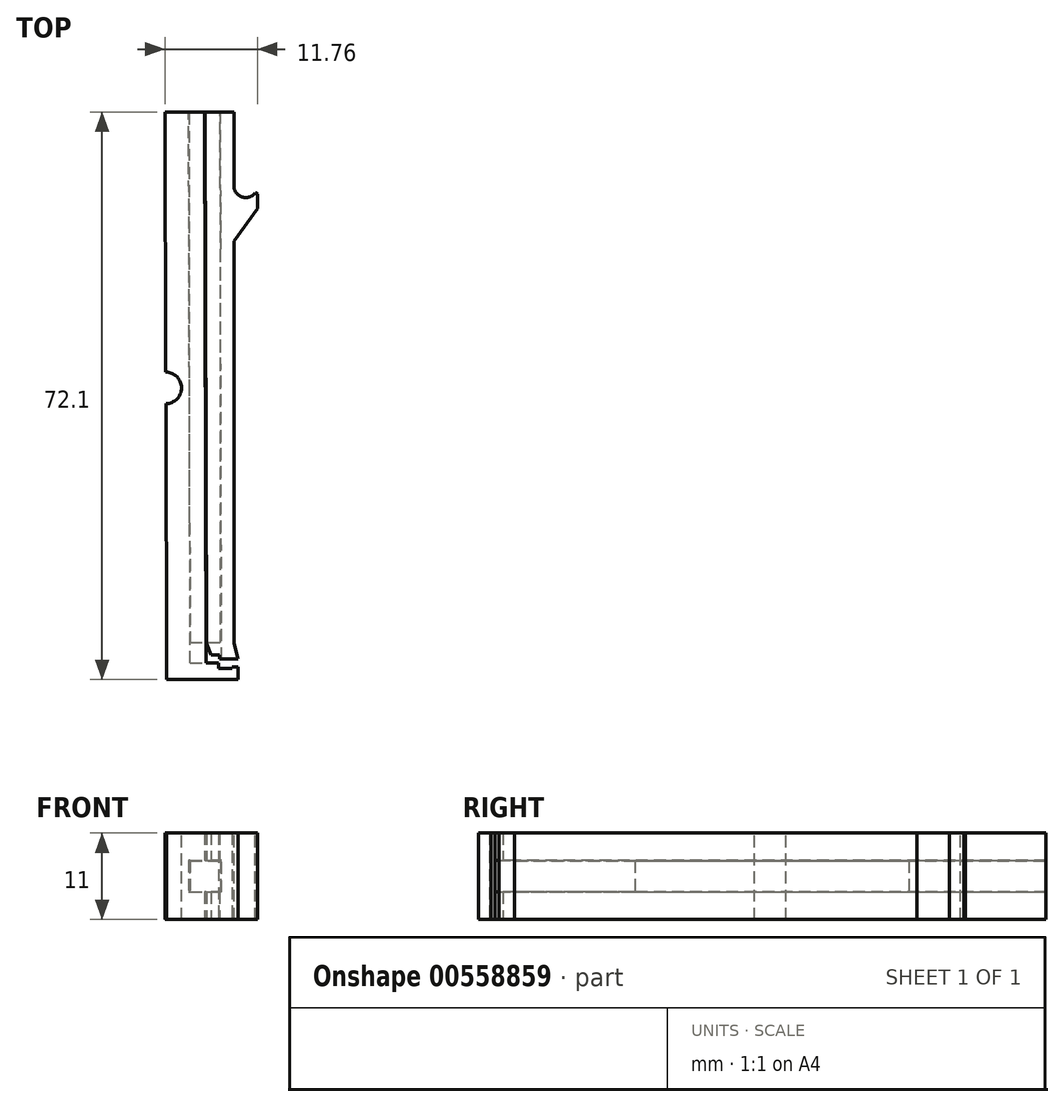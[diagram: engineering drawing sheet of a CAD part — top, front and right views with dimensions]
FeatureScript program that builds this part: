
annotation { "Feature Type Name" : "Feature", "Feature Type Description" : "" }
export const myFeature = defineFeature(function(context is Context, id is Id, definition is map)
    precondition{}
    {
        {
            var Q0;
            Q0=qCreatedBy(makeId("Top.planeOp"),FACE);
            var sketch = newSketch(context, id + "F0", { "sketchPlane" : qUnion([Q0])});
            skLineSegment(sketch, "E0", {"start": v(-25.83, -4.71) * mm, "end": v(-26.63, -4.71) * mm});
            skLineSegment(sketch, "E1", {"start": v(-25.84, -3.71) * mm, "end": v(-28.23, -3.71) * mm});
            skLineSegment(sketch, "E2", {"start": v(-25.83, -4.71) * mm, "end": v(-25.83, -6.31) * mm});
            skLineSegment(sketch, "E3", {"start": v(-26.63, -4.71) * mm, "end": v(-26.63, -4.91) * mm});
            skLineSegment(sketch, "E4", {"start": v(-26.63, -4.91) * mm, "end": v(-28.33, -4.91) * mm});
            skLineSegment(sketch, "E5", {"start": v(-28.33, -4.91) * mm, "end": v(-28.33, -4.71) * mm});
            skLineSegment(sketch, "E6", {"start": v(-25.84, -3.71) * mm, "end": v(-26.38, -1.71) * mm});
            skLineSegment(sketch, "E7", {"start": v(-25.83, -6.31) * mm, "end": v(-31.04, -6.31) * mm});
            skLineSegment(sketch, "E8", {"start": v(-28.33, -4.71) * mm, "end": v(-28.33, -4.21) * mm});
            skLineSegment(sketch, "E9", {"start": v(-28.33, -4.21) * mm, "end": v(-29.93, -4.21) * mm});
            skLineSegment(sketch, "E10", {"start": v(-28.23, -3.71) * mm, "end": v(-28.23, -3.21) * mm});
            skLineSegment(sketch, "E11", {"start": v(-28.23, -3.21) * mm, "end": v(-29.28, -3.21) * mm});
            skLineSegment(sketch, "E12", {"start": v(-29.93, -4.21) * mm, "end": v(-30.14, 65.79) * mm});
            skLineSegment(sketch, "E13", {"start": v(-30.14, 65.79) * mm, "end": v(-35.14, 65.77) * mm});
            skLineSegment(sketch, "E14", {"start": v(-35.14, 65.77) * mm, "end": v(-34.93, -6.31) * mm});
            skLineSegment(sketch, "E15", {"start": v(-34.93, -6.31) * mm, "end": v(-31.04, -6.31) * mm});
            skPoint(sketch, "E16.trimOffspring.end.orphan", {"position": v(-30.14, -4.71) * mm});
            skLineSegment(sketch, "E17", {"start": v(-26.38, -1.71) * mm, "end": v(-26.38, 65.79) * mm});
            skLineSegment(sketch, "E18", {"start": v(-26.38, 65.79) * mm, "end": v(-30.04, 65.79) * mm});
            skLineSegment(sketch, "E19", {"start": v(-30.04, 65.79) * mm, "end": v(-29.84, -1.71) * mm});
            skLineSegment(sketch, "E20", {"start": v(-29.84, -1.71) * mm, "end": v(-29.28, -3.21) * mm});
            skPoint(sketch, "E21.end.orphan", {"position": v(-29.32, -1.71) * mm});
            skSolve(sketch);
        }
        {
            var Q0;
            Q0 = qSketchRegion(id + "F0", true);
            extrude(context, id + "F1", {"entities" : qUnion([Q0]), "depth" : 11 * mm, "offsetDistance" : 25 * mm});
        }
        {
            var Q0;
            Q0=makeQuery(id+"F1.opExtrude","SWEPT_FACE",FACE,{"disambiguationData":[OSD([sQuery(id+"F0.wireOp",EDGE,"E13")])]});
            var sketch = newSketch(context, id + "F2", { "sketchPlane" : qUnion([Q0])});
            skLineSegment(sketch, "E22.bottom", {"start": v(31.95, 7.5) * mm, "end": v(27.95, 7.5) * mm});
            skLineSegment(sketch, "E22.top", {"start": v(31.95, 3.5) * mm, "end": v(27.95, 3.5) * mm});
            skLineSegment(sketch, "E22.left", {"start": v(31.95, 7.5) * mm, "end": v(31.95, 3.5) * mm});
            skLineSegment(sketch, "E22.right", {"start": v(27.95, 7.5) * mm, "end": v(27.95, 3.5) * mm});
            skPoint(sketch, "E22.middle", {"position": v(29.95, 5.5) * mm});
            skSolve(sketch);
        }
        {
            var Q0;
            Q0 = qSketchRegion(id + "F2", true);
            var Q1;
            Q1=makeQuery(id+"F1.opExtrude","SWEPT_FACE",FACE,{"disambiguationData":[OSD([sQuery(id+"F0.wireOp",EDGE,"E9")])]});
            extrude(context, id + "F3", {"entities" : qUnion([Q0]), "operationType" : NewBodyOperationType.REMOVE, "endBound" : BoundingType.UP_TO_SURFACE, "oppositeDirection" : true, "depth" : 69.93 * mm, "endBoundEntityFace" : qUnion([Q1]), "offsetDistance" : 25 * mm});
        }
        {
            var Q0;
            Q0=makeQuery(id+"F1.opExtrude","SWEPT_FACE",FACE,{"disambiguationData":[OSD([sQuery(id+"F0.wireOp",EDGE,"E18")])]});
            var sketch = newSketch(context, id + "F4", { "sketchPlane" : qUnion([Q0])});
            skLineSegment(sketch, "E23.bottom", {"start": v(31.99, 7.45) * mm, "end": v(28.09, 7.45) * mm});
            skLineSegment(sketch, "E23.top", {"start": v(31.99, 3.55) * mm, "end": v(28.09, 3.55) * mm});
            skLineSegment(sketch, "E23.left", {"start": v(31.99, 7.45) * mm, "end": v(31.99, 3.55) * mm});
            skLineSegment(sketch, "E23.right", {"start": v(28.09, 7.45) * mm, "end": v(28.09, 3.55) * mm});
            skPoint(sketch, "E23.middle", {"position": v(30.04, 5.5) * mm});
            skSolve(sketch);
        }
        {
            var Q0;
            Q0 = qSketchRegion(id + "F4", true);
            extrude(context, id + "F5", {"entities" : qUnion([Q0]), "operationType" : NewBodyOperationType.ADD, "oppositeDirection" : true, "depth" : 67.39 * mm, "offsetDistance" : 25 * mm});
        }
        {
            var Q0;
            Q0=makeQuery(id+"F1.opExtrude","CAP_FACE",FACE,{"disambiguationData":[OSD([sQuery(id+"F0.wireOp",EDGE,"E0"),sQuery(id+"F0.wireOp",EDGE,"E2"),sQuery(id+"F0.wireOp",EDGE,"E3"),sQuery(id+"F0.wireOp",EDGE,"E4"),sQuery(id+"F0.wireOp",EDGE,"E5"),sQuery(id+"F0.wireOp",EDGE,"E7"),sQuery(id+"F0.wireOp",EDGE,"E8"),sQuery(id+"F0.wireOp",EDGE,"E9"),sQuery(id+"F0.wireOp",EDGE,"E12"),sQuery(id+"F0.wireOp",EDGE,"E13"),sQuery(id+"F0.wireOp",EDGE,"E14"),sQuery(id+"F0.wireOp",EDGE,"E15")])],"isStart":false});
            var sketch = newSketch(context, id + "F6", { "sketchPlane" : qUnion([Q0])});
            skCircle(sketch, "E24", {"center": v(-35.03, 30.74) * mm, "radius": 2 * mm});
            skSolve(sketch);
        }
        {
            var Q0;
            Q0 = qSketchRegion(id + "F6", true);
            extrude(context, id + "F7", {"entities" : qUnion([Q0]), "operationType" : NewBodyOperationType.REMOVE, "oppositeDirection" : true, "depth" : 25 * mm, "offsetDistance" : 25 * mm});
        }
        {
            var Q0;
            Q0=makeQuery(id+"F1.opExtrude","CAP_FACE",FACE,{"disambiguationData":[OSD([sQuery(id+"F0.wireOp",EDGE,"E1"),sQuery(id+"F0.wireOp",EDGE,"E6"),sQuery(id+"F0.wireOp",EDGE,"E10"),sQuery(id+"F0.wireOp",EDGE,"E11"),sQuery(id+"F0.wireOp",EDGE,"E17"),sQuery(id+"F0.wireOp",EDGE,"E18"),sQuery(id+"F0.wireOp",EDGE,"E19"),sQuery(id+"F0.wireOp",EDGE,"E20")])],"isStart":false});
            var sketch = newSketch(context, id + "F8", { "sketchPlane" : qUnion([Q0])});
            skArc(sketch, "E25", {"start": v(-26.38, 56.41) * mm, "mid": v(-25.35, 54.99) * mm, "end": v(-23.67, 55.52) * mm});
            skLineSegment(sketch, "E26", {"start": v(-23.38, 53.51) * mm, "end": v(-26.38, 49.38) * mm});
            skLineSegment(sketch, "E27", {"start": v(-26.38, 49.38) * mm, "end": v(-26.38, 56.41) * mm});
            skLineSegment(sketch, "E28", {"start": v(-23.67, 55.52) * mm, "end": v(-23.38, 55.38) * mm});
            skLineSegment(sketch, "E29.trimOffspring", {"start": v(-23.38, 55.38) * mm, "end": v(-23.38, 53.51) * mm});
            skSolve(sketch);
        }
        {
            var Q0;
            Q0 = qSketchRegion(id + "F8", true);
            var Q1;
            Q1=makeQuery(id+"F1.opExtrude","CAP_FACE",FACE,{"disambiguationData":[OSD([sQuery(id+"F0.wireOp",EDGE,"E1"),sQuery(id+"F0.wireOp",EDGE,"E6"),sQuery(id+"F0.wireOp",EDGE,"E10"),sQuery(id+"F0.wireOp",EDGE,"E11"),sQuery(id+"F0.wireOp",EDGE,"E17"),sQuery(id+"F0.wireOp",EDGE,"E18"),sQuery(id+"F0.wireOp",EDGE,"E19"),sQuery(id+"F0.wireOp",EDGE,"E20")])],"isStart":true});
            extrude(context, id + "F9", {"entities" : qUnion([Q0]), "operationType" : NewBodyOperationType.ADD, "endBound" : BoundingType.UP_TO_SURFACE, "oppositeDirection" : true, "depth" : 25 * mm, "endBoundEntityFace" : qUnion([Q1]), "offsetDistance" : 25 * mm});
        }
    });
